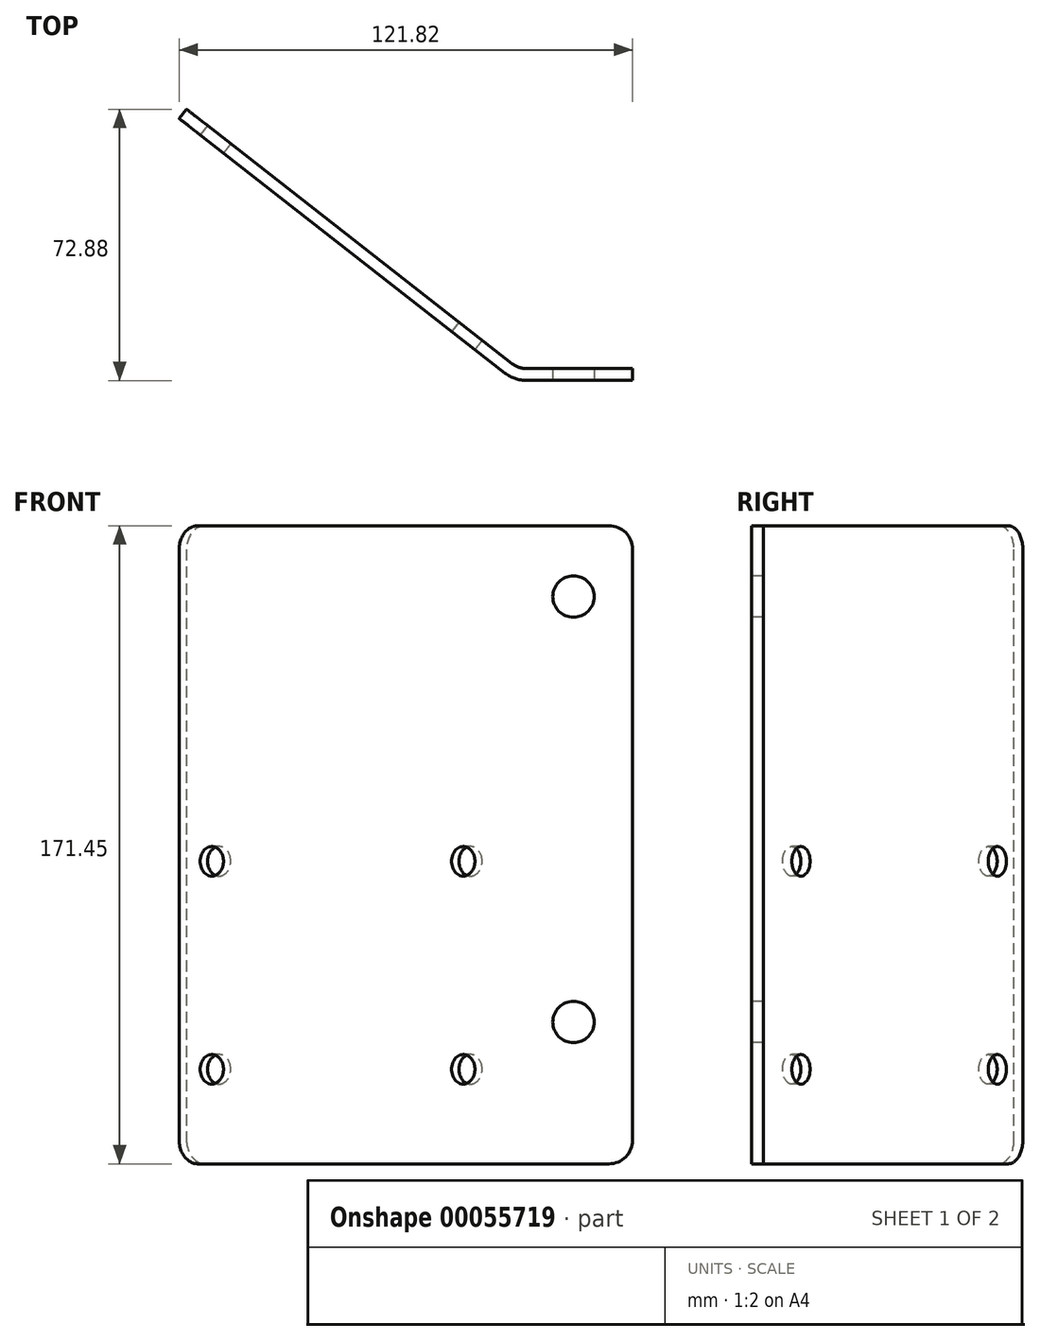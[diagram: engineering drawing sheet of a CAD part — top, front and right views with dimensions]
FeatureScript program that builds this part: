
annotation { "Feature Type Name" : "Feature", "Feature Type Description" : "" }
export const myFeature = defineFeature(function(context is Context, id is Id, definition is map)
    precondition{}
    {
        {
            var Q0;
            Q0=qCreatedBy(makeId("Top.planeOp"),FACE);
            var sketch = newSketch(context, id + "F0", { "sketchPlane" : qUnion([Q0])});
            skLineSegment(sketch, "E0", {"start": v(0, 0) * mm, "end": v(-28.47, 0) * mm});
            skArc(sketch, "E1", {"start": v(-32.38, 1.35) * mm, "mid": v(-30.54, 0.35) * mm, "end": v(-28.47, 0) * mm});
            skLineSegment(sketch, "E2", {"start": v(-32.38, 1.35) * mm, "end": v(-119.86, 69.7) * mm});
            skLineSegment(sketch, "E3.0", {"start": v(-34.33, -1.16) * mm, "end": v(-121.82, 67.2) * mm});
            skArc(sketch, "E3.1", {"start": v(-34.33, -1.16) * mm, "mid": v(-31.57, -2.66) * mm, "end": v(-28.47, -3.18) * mm});
            skLineSegment(sketch, "E3.2", {"start": v(0, -3.17) * mm, "end": v(-28.47, -3.17) * mm});
            skLineSegment(sketch, "E4", {"start": v(0, 0) * mm, "end": v(0, -3.17) * mm});
            skLineSegment(sketch, "E5", {"start": v(-119.86, 69.7) * mm, "end": v(-121.82, 67.2) * mm});
            skPoint(sketch, "E6", {"position": v(-31.75, -3.17) * mm});
            skSolve(sketch);
        }
        {
            var Q0;
            Q0 = qSketchRegion(id + "F0", true);
            extrude(context, id + "F1", {"entities" : qUnion([Q0]), "depth" : 171.45 * mm});
        }
        {
            var Q0;
            Q0=makeQuery(id+"F1.opExtrude","SWEPT_FACE",FACE,{"disambiguationData":[OSD([sQuery(id+"F0.wireOp",EDGE,"E3.2")])]});
            var sketch = newSketch(context, id + "F2", { "sketchPlane" : qUnion([Q0])});
            skCircle(sketch, "E7", {"center": v(-15.88, 152.4) * mm, "radius": 5.56 * mm});
            skCircle(sketch, "E8", {"center": v(-15.88, 38.1) * mm, "radius": 5.56 * mm});
            skSolve(sketch);
        }
        {
            var Q0;
            Q0 = qSketchRegion(id + "F2", true);
            extrude(context, id + "F3", {"entities" : qUnion([Q0]), "operationType" : NewBodyOperationType.REMOVE, "endBound" : BoundingType.THROUGH_ALL, "oppositeDirection" : true, "depth" : 25.4 * mm});
        }
        {
            var Q0;
            Q0=makeQuery(id+"F1.opExtrude","SWEPT_FACE",FACE,{"disambiguationData":[OSD([sQuery(id+"F0.wireOp",EDGE,"E3.0")])]});
            var sketch = newSketch(context, id + "F4", { "sketchPlane" : qUnion([Q0])});
            skCircle(sketch, "E9", {"center": v(-126.24, 81.28) * mm, "radius": 3.98 * mm});
            skCircle(sketch, "E10", {"center": v(-40.51, 81.28) * mm, "radius": 3.98 * mm});
            skCircle(sketch, "E11", {"center": v(-40.51, 25.4) * mm, "radius": 3.98 * mm});
            skCircle(sketch, "E12", {"center": v(-126.24, 25.4) * mm, "radius": 3.98 * mm});
            skSolve(sketch);
        }
        {
            var Q0;
            Q0 = qSketchRegion(id + "F4", true);
            extrude(context, id + "F5", {"entities" : qUnion([Q0]), "operationType" : NewBodyOperationType.REMOVE, "endBound" : BoundingType.THROUGH_ALL, "oppositeDirection" : true, "depth" : 25.4 * mm});
        }
        {
            var Q0;
            Q0=makeQuery(id+"F1.opExtrude","CAP_EDGE",EDGE,{"disambiguationData":[OSD([sQuery(id+"F0.wireOp",EDGE,"E5")])],"isStart":false});
            var Q1;
            Q1=makeQuery(id+"F1.opExtrude","CAP_EDGE",EDGE,{"disambiguationData":[OSD([sQuery(id+"F0.wireOp",EDGE,"E5")])],"isStart":true});
            var Q2;
            Q2=makeQuery(id+"F1.opExtrude","CAP_EDGE",EDGE,{"disambiguationData":[OSD([sQuery(id+"F0.wireOp",EDGE,"E4")])],"isStart":false});
            var Q3;
            Q3=makeQuery(id+"F1.opExtrude","CAP_EDGE",EDGE,{"disambiguationData":[OSD([sQuery(id+"F0.wireOp",EDGE,"E4")])],"isStart":true});
            fillet(context, id + "F6", {"entities" : qUnion([Q0, Q1, Q2, Q3]), "radius" : 6.35 * mm, "tangentPropagation" : true, "allowEdgeOverflow" : false});
        }
    });
